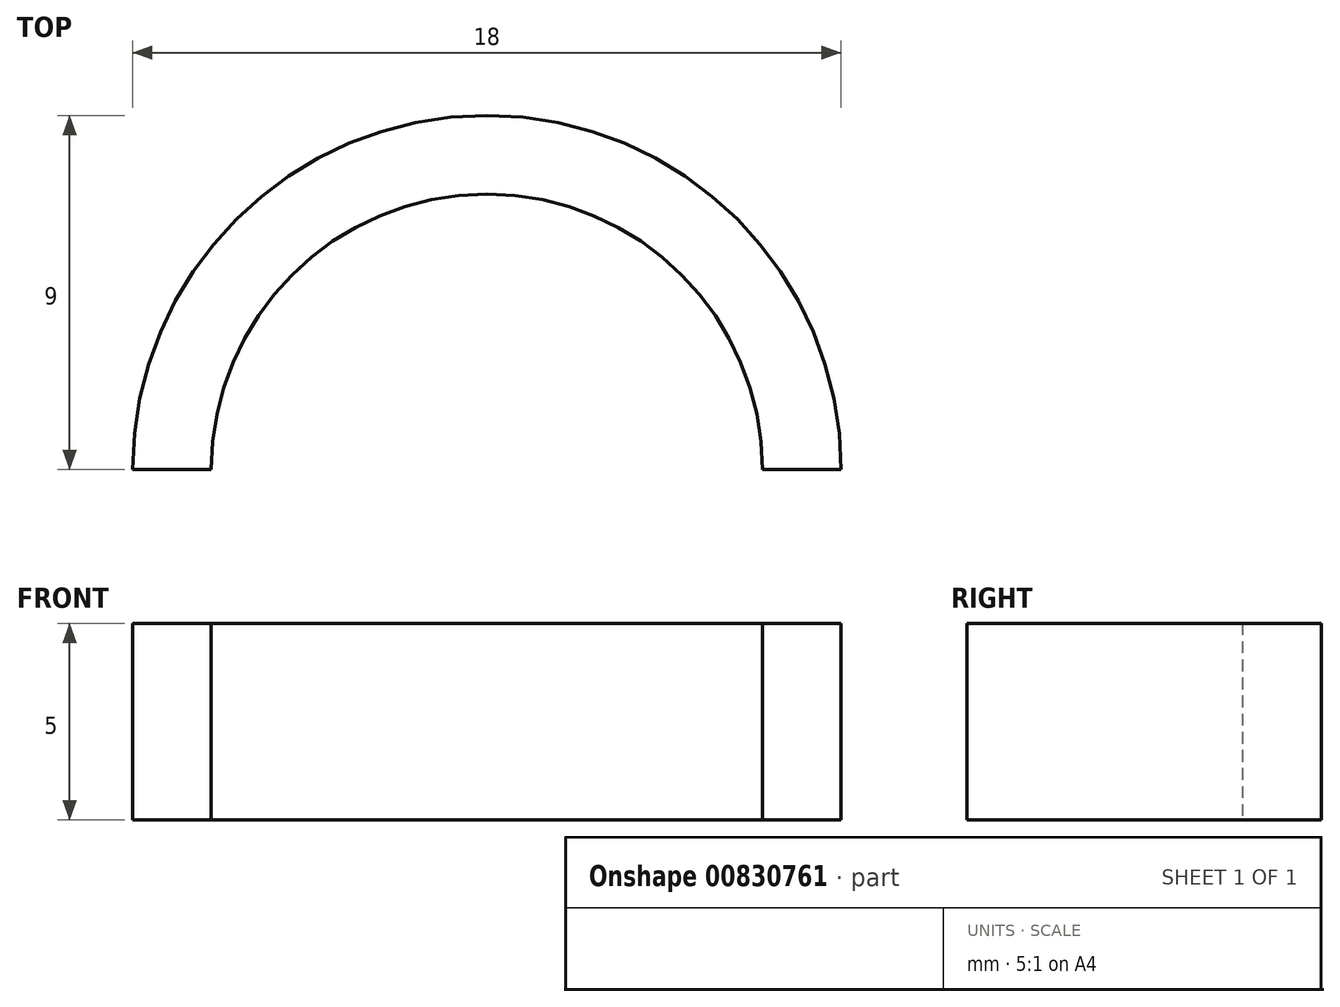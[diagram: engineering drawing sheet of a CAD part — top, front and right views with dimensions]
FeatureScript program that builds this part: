
annotation { "Feature Type Name" : "Feature", "Feature Type Description" : "" }
export const myFeature = defineFeature(function(context is Context, id is Id, definition is map)
    precondition{}
    {
        {
            var Q0;
            Q0=qCreatedBy(makeId("Top.planeOp"),FACE);
            var sketch = newSketch(context, id + "F0", { "sketchPlane" : qUnion([Q0])});
            skCircle(sketch, "E0", {"center": v(0, 0) * mm, "radius": 9 * mm});
            skCircle(sketch, "E1", {"center": v(0, 0) * mm, "radius": 7 * mm});
            skSolve(sketch);
        }
        {
            var Q0;
            Q0=makeQuery(id+"F0.imprint","IMPRINT",FACE,{"disambiguationData":[TD([[makeQuery(id+"F0.imprint","IMPRINT",EDGE,{"derivedFrom":sQuery(id+"F0.wireOp",EDGE,"E0")}),1.0]])]});
            extrude(context, id + "F1", {"entities" : qUnion([Q0]), "depth" : 5 * mm, "offsetDistance" : 25 * mm});
        }
        {
            var Q0;
            Q0=makeQuery(id+"F1.opExtrude","CAP_FACE",FACE,{"disambiguationData":[OSD([sQuery(id+"F0.wireOp",EDGE,"E0"),sQuery(id+"F0.wireOp",EDGE,"E1")])],"isStart":false});
            var sketch = newSketch(context, id + "F2", { "sketchPlane" : qUnion([Q0])});
            skLineSegment(sketch, "E2.bottom", {"start": v(-21.27, -17.77) * mm, "end": v(16.1, -17.77) * mm});
            skLineSegment(sketch, "E2.top", {"start": v(-21.27, 0) * mm, "end": v(16.1, 0) * mm});
            skLineSegment(sketch, "E2.left", {"start": v(-21.27, -17.77) * mm, "end": v(-21.27, 0) * mm});
            skLineSegment(sketch, "E2.right", {"start": v(16.1, -17.77) * mm, "end": v(16.1, 0) * mm});
            skSolve(sketch);
        }
        {
            var Q0;
            {var subQ0=sQuery(id+"F2.wireOp",EDGE,"E2.top");var subQ1=makeQuery(id+"F1.opExtrude","CAP_EDGE",EDGE,{"disambiguationData":[OSD([sQuery(id+"F0.wireOp",EDGE,"E0")])],"isStart":false});var subQ2=makeQuery(id+"F2.imprint","INTERSECT",VERTEX,{"disambiguationData":[OD(0.0)],"derivedFrom":[subQ1,subQ0]});Q0=makeQuery(id+"F2.imprint","IMPRINT",FACE,{"disambiguationData":[TD([[makeQuery(id+"F2.imprint","IMPRINT",EDGE,{"disambiguationData":[TD([[subQ2,-1.0]])],"derivedFrom":subQ0}),-1.0]])]});}
            extrude(context, id + "F3", {"entities" : qUnion([Q0]), "operationType" : NewBodyOperationType.REMOVE, "oppositeDirection" : true, "depth" : 25 * mm, "offsetDistance" : 25 * mm});
        }
    });
